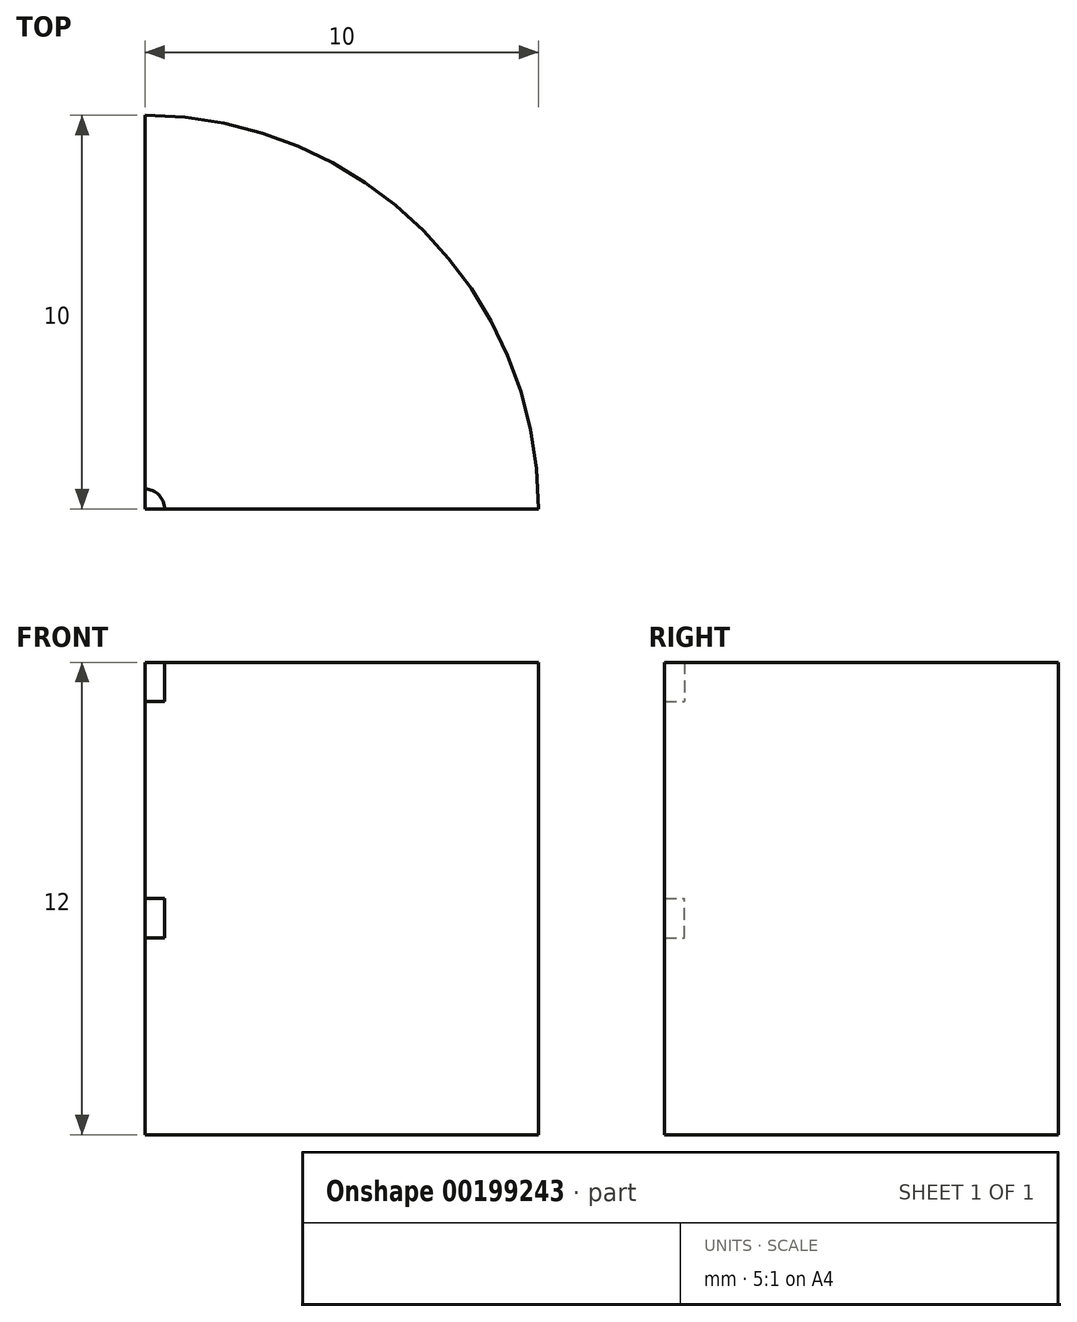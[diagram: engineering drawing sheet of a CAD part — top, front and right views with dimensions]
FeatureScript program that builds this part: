
annotation { "Feature Type Name" : "Feature", "Feature Type Description" : "" }
export const myFeature = defineFeature(function(context is Context, id is Id, definition is map)
    precondition{}
    {
        {
            var Q0;
            Q0=qCreatedBy(makeId("Top.planeOp"),FACE);
            var sketch = newSketch(context, id + "F0", { "sketchPlane" : qUnion([Q0])});
            skCircle(sketch, "E0", {"center": v(0, 0) * mm, "radius": 0.5 * mm});
            skCircle(sketch, "E1", {"center": v(0, 0) * mm, "radius": 1.25 * mm});
            skCircle(sketch, "E2", {"center": v(0, 0) * mm, "radius": 10 * mm});
            skLineSegment(sketch, "E3", {"start": v(0, 0) * mm, "end": v(10, 0) * mm});
            skLineSegment(sketch, "E4", {"start": v(0, 0) * mm, "end": v(0, 10) * mm});
            skSolve(sketch);
        }
        {
            assignVariable(context, id + "F1", {"name" : "h0", "anyValue" : 1});
        }
        {
            assignVariable(context, id + "F2", {"name" : "htotal", "anyValue" : 6});
        }
        {
            var Q0;
            {var subQ0=sQuery(id+"F0.wireOp",EDGE,"E3");var subQ1=sQuery(id+"F0.wireOp",EDGE,"E1");var subQ2=makeQuery(id+"F0.imprint","INTERSECT",VERTEX,{"derivedFrom":[subQ1,subQ0]});Q0=makeQuery(id+"F0.imprint","IMPRINT",FACE,{"disambiguationData":[TD([[makeQuery(id+"F0.imprint","IMPRINT",EDGE,{"disambiguationData":[TD([[subQ2,-1.0]])],"derivedFrom":subQ1}),-1.0]])]});}
            var Q1;
            {var subQ0=sQuery(id+"F0.wireOp",EDGE,"E3");var subQ1=sQuery(id+"F0.wireOp",EDGE,"E0");var subQ2=makeQuery(id+"F0.imprint","INTERSECT",VERTEX,{"derivedFrom":[subQ1,subQ0]});Q1=makeQuery(id+"F0.imprint","IMPRINT",FACE,{"disambiguationData":[TD([[makeQuery(id+"F0.imprint","IMPRINT",EDGE,{"disambiguationData":[TD([[subQ2,-1.0]])],"derivedFrom":subQ1}),-1.0]])]});}
            var Q2;
            {var subQ0=sQuery(id+"F0.wireOp",EDGE,"E3");var subQ1=sQuery(id+"F0.wireOp",EDGE,"E0");var subQ2=makeQuery(id+"F0.imprint","INTERSECT",VERTEX,{"derivedFrom":[subQ1,subQ0]});Q2=makeQuery(id+"F0.imprint","IMPRINT",FACE,{"disambiguationData":[TD([[makeQuery(id+"F0.imprint","IMPRINT",EDGE,{"disambiguationData":[TD([[subQ2,-1.0]])],"derivedFrom":subQ1}),1.0]])]});}
            extrude(context, id + "F3", {"entities" : qUnion([Q0, Q1, Q2]), "oppositeDirection" : true, "depth" : (getVariable(context, 'htotal')) * mm});
        }
        {
            var Q0;
            {var subQ0=sQuery(id+"F0.wireOp",EDGE,"E3");var subQ1=sQuery(id+"F0.wireOp",EDGE,"E0");var subQ2=makeQuery(id+"F0.imprint","INTERSECT",VERTEX,{"derivedFrom":[subQ1,subQ0]});Q0=makeQuery(id+"F0.imprint","IMPRINT",FACE,{"disambiguationData":[TD([[makeQuery(id+"F0.imprint","IMPRINT",EDGE,{"disambiguationData":[TD([[subQ2,-1.0]])],"derivedFrom":subQ1}),1.0]])]});}
            extrude(context, id + "F4", {"entities" : qUnion([Q0]), "operationType" : NewBodyOperationType.REMOVE, "oppositeDirection" : true, "depth" : (getVariable(context, 'h0')) * mm});
        }
        {
            var Q0;
            {var subQ0=sQuery(id+"F0.wireOp",EDGE,"E3");var subQ1=sQuery(id+"F0.wireOp",EDGE,"E1");var subQ2=makeQuery(id+"F0.imprint","INTERSECT",VERTEX,{"derivedFrom":[subQ1,subQ0]});Q0=makeQuery(id+"F0.imprint","IMPRINT",FACE,{"disambiguationData":[TD([[makeQuery(id+"F0.imprint","IMPRINT",EDGE,{"disambiguationData":[TD([[subQ2,-1.0]])],"derivedFrom":subQ1}),-1.0]])]});}
            var Q1;
            {var subQ0=sQuery(id+"F0.wireOp",EDGE,"E3");var subQ1=sQuery(id+"F0.wireOp",EDGE,"E0");var subQ2=makeQuery(id+"F0.imprint","INTERSECT",VERTEX,{"derivedFrom":[subQ1,subQ0]});Q1=makeQuery(id+"F0.imprint","IMPRINT",FACE,{"disambiguationData":[TD([[makeQuery(id+"F0.imprint","IMPRINT",EDGE,{"disambiguationData":[TD([[subQ2,-1.0]])],"derivedFrom":subQ1}),-1.0]])]});}
            extrude(context, id + "F5", {"entities" : qUnion([Q0, Q1]), "depth" : (getVariable(context, 'htotal')) * mm});
        }
        {
            var Q0;
            {var subQ0=sQuery(id+"F0.wireOp",EDGE,"E3");var subQ1=sQuery(id+"F0.wireOp",EDGE,"E0");var subQ2=makeQuery(id+"F0.imprint","INTERSECT",VERTEX,{"derivedFrom":[subQ1,subQ0]});Q0=makeQuery(id+"F0.imprint","IMPRINT",FACE,{"disambiguationData":[TD([[makeQuery(id+"F0.imprint","IMPRINT",EDGE,{"disambiguationData":[TD([[subQ2,-1.0]])],"derivedFrom":subQ1}),1.0]])]});}
            extrude(context, id + "F6", {"entities" : qUnion([Q0]), "operationType" : NewBodyOperationType.ADD, "depth" : (getVariable(context, 'htotal') - getVariable(context, 'h0')) * mm});
        }
    });
